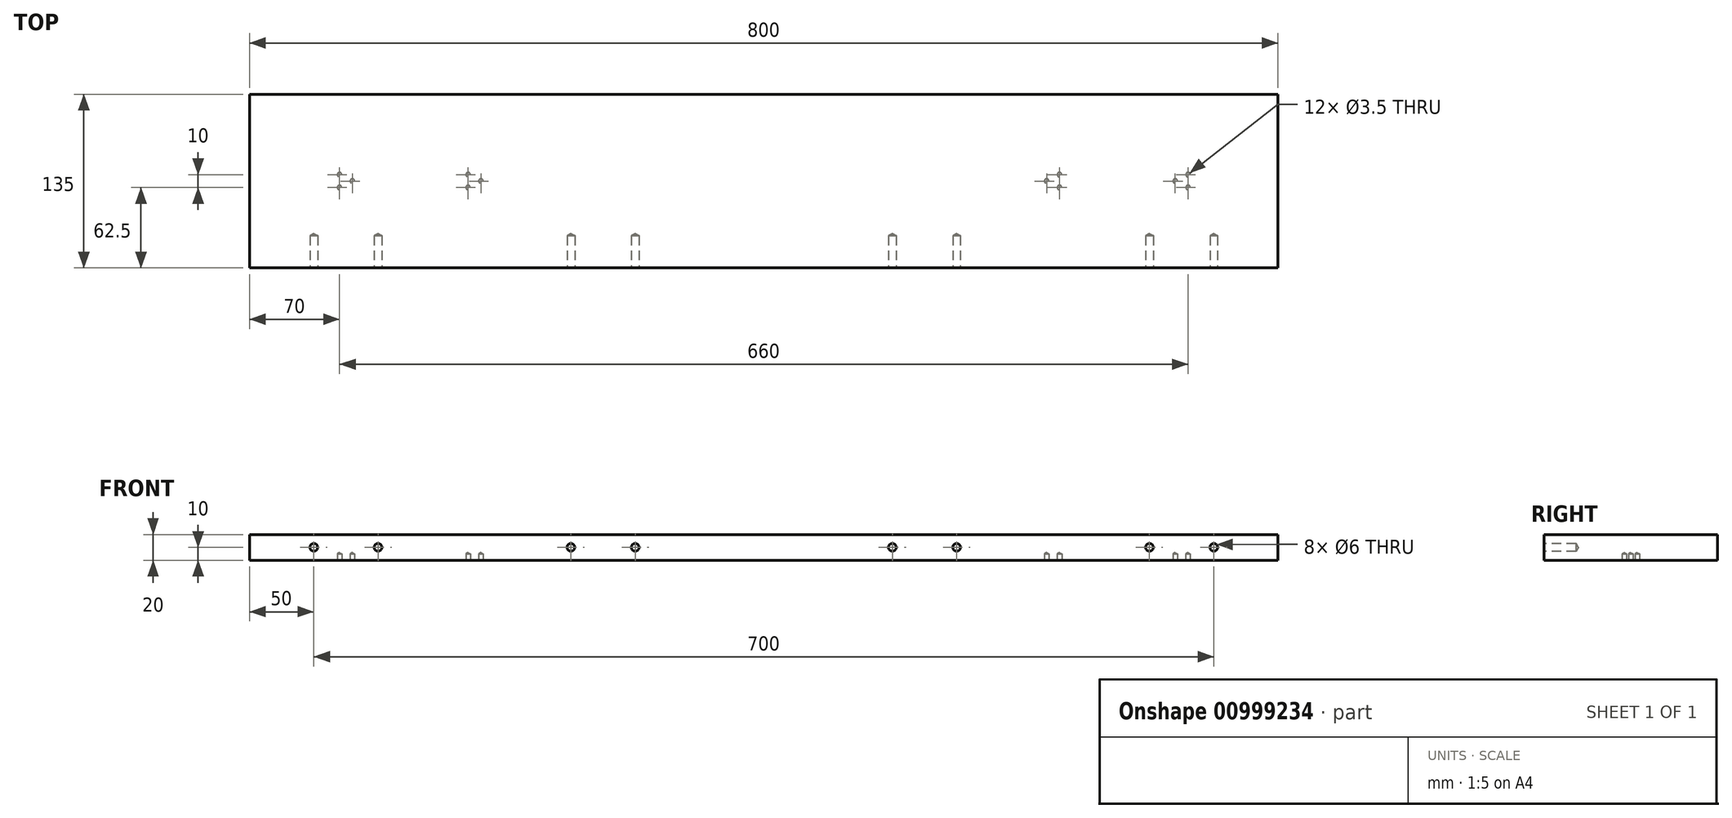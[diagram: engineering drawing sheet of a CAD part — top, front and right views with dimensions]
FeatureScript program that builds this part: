
annotation { "Feature Type Name" : "Feature", "Feature Type Description" : "" }
export const myFeature = defineFeature(function(context is Context, id is Id, definition is map)
    precondition{}
    {
        {
            var Q0;
            Q0=qCreatedBy(makeId("Top.planeOp"),FACE);
            var sketch = newSketch(context, id + "F0", { "sketchPlane" : qUnion([Q0])});
            skLineSegment(sketch, "E0.bottom", {"start": v(400, 67.5) * mm, "end": v(-400, 67.5) * mm});
            skLineSegment(sketch, "E0.top", {"start": v(400, -67.5) * mm, "end": v(-400, -67.5) * mm});
            skLineSegment(sketch, "E0.left", {"start": v(400, 67.5) * mm, "end": v(400, -67.5) * mm});
            skLineSegment(sketch, "E0.right", {"start": v(-400, 67.5) * mm, "end": v(-400, -67.5) * mm});
            skPoint(sketch, "E0.middle", {"position": v(0, 0) * mm});
            skSolve(sketch);
        }
        {
            var Q0;
            Q0=qSketchRegion(id+"F0",true);
            extrude(context, id + "F1", {"entities" : qUnion([Q0]), "endBound" : BoundingType.SYMMETRIC, "depth" : 20 * mm, "offsetDistance" : 25 * mm});
        }
        {
            var Q0;
            Q0=makeQuery(id+"F1.opExtrude","SWEPT_FACE",FACE,{"disambiguationData":[OSD([sQuery(id+"F0.wireOp",EDGE,"E0.top")])]});
            var sketch = newSketch(context, id + "F2", { "sketchPlane" : qUnion([Q0])});
            skPoint(sketch, "E1", {"position": v(-350, 0) * mm});
            skPoint(sketch, "E2", {"position": v(-100, 0) * mm});
            skPoint(sketch, "E3", {"position": v(-150, 0) * mm});
            skPoint(sketch, "E4", {"position": v(-300, 0) * mm});
            skPoint(sketch, "E5.MirrorP", {"position": v(350, 0) * mm});
            skPoint(sketch, "E6.MirrorP", {"position": v(300, 0) * mm});
            skPoint(sketch, "E7.MirrorP", {"position": v(150, 0) * mm});
            skPoint(sketch, "E8.MirrorP", {"position": v(100, 0) * mm});
            skSolve(sketch);
        }
        {
            var Q0;
            Q0=sQuery(id+"F2.wireOp",VERTEX,"E1");
            var Q1;
            Q1=sQuery(id+"F2.wireOp",VERTEX,"E4");
            var Q2;
            Q2=sQuery(id+"F2.wireOp",VERTEX,"E3");
            var Q3;
            Q3=sQuery(id+"F2.wireOp",VERTEX,"E2");
            var Q4;
            Q4=sQuery(id+"F2.wireOp",VERTEX,"E8.MirrorP");
            var Q5;
            Q5=sQuery(id+"F2.wireOp",VERTEX,"E7.MirrorP");
            var Q6;
            Q6=sQuery(id+"F2.wireOp",VERTEX,"E6.MirrorP");
            var Q7;
            Q7=sQuery(id+"F2.wireOp",VERTEX,"E5.MirrorP");
            var Q8;
            Q8=makeQuery(id+"F1.opExtrude","SWEPT_BODY",BODY,{"disambiguationData":[OSD([sQuery(id+"F0.wireOp",EDGE,"E0.bottom"),sQuery(id+"F0.wireOp",EDGE,"E0.top"),sQuery(id+"F0.wireOp",EDGE,"E0.left"),sQuery(id+"F0.wireOp",EDGE,"E0.right")])]});
            hole(context, id + "F3", {"style" : HoleStyle.SIMPLE, "endStyle" : HoleEndStyle.BLIND, "holeDiameter" : 6 * mm, "majorDiameter" : 5 * mm, "holeDepth" : 25 * mm, "isTappedThrough" : true, "tappedDepth" : 12 * mm, "tapClearance" : 3, "locations" : qUnion([Q0, Q1, Q2, Q3, Q4, Q5, Q6, Q7]), "scope" : qUnion([Q8])});
        }
        {
            var Q0;
            Q0=makeQuery(id+"F1.opExtrude","CAP_FACE",FACE,{"disambiguationData":[OSD([sQuery(id+"F0.wireOp",EDGE,"E0.bottom"),sQuery(id+"F0.wireOp",EDGE,"E0.top"),sQuery(id+"F0.wireOp",EDGE,"E0.left"),sQuery(id+"F0.wireOp",EDGE,"E0.right")])],"isStart":true});
            var sketch = newSketch(context, id + "F4", { "sketchPlane" : qUnion([Q0])});
            skPoint(sketch, "E9", {"position": v(-330, 5) * mm});
            skPoint(sketch, "E10", {"position": v(-330, -5) * mm});
            skPoint(sketch, "E11", {"position": v(-320, 0) * mm});
            skPoint(sketch, "E12", {"position": v(-230, 5) * mm});
            skPoint(sketch, "E13", {"position": v(-230, -5) * mm});
            skPoint(sketch, "E14", {"position": v(-220, 0) * mm});
            skPoint(sketch, "E15.MirrorP", {"position": v(330, 5) * mm});
            skPoint(sketch, "E16.MirrorP", {"position": v(330, -5) * mm});
            skPoint(sketch, "E17.MirrorP", {"position": v(320, 0) * mm});
            skPoint(sketch, "E18.MirrorP", {"position": v(230, 5) * mm});
            skPoint(sketch, "E19.MirrorP", {"position": v(230, -5) * mm});
            skPoint(sketch, "E20.MirrorP", {"position": v(220, 0) * mm});
            skSolve(sketch);
        }
        {
            var Q0;
            Q0=sQuery(id+"F4.wireOp",VERTEX,"E9");
            var Q1;
            Q1=sQuery(id+"F4.wireOp",VERTEX,"E10");
            var Q2;
            Q2=sQuery(id+"F4.wireOp",VERTEX,"E11");
            var Q3;
            Q3=sQuery(id+"F4.wireOp",VERTEX,"E12");
            var Q4;
            Q4=sQuery(id+"F4.wireOp",VERTEX,"E13");
            var Q5;
            Q5=sQuery(id+"F4.wireOp",VERTEX,"E14");
            var Q6;
            Q6=makeQuery(id+"F1.opExtrude","SWEPT_BODY",BODY,{"disambiguationData":[OSD([sQuery(id+"F0.wireOp",EDGE,"E0.bottom"),sQuery(id+"F0.wireOp",EDGE,"E0.top"),sQuery(id+"F0.wireOp",EDGE,"E0.left"),sQuery(id+"F0.wireOp",EDGE,"E0.right")])]});
            hole(context, id + "F5", {"style" : HoleStyle.SIMPLE, "endStyle" : HoleEndStyle.BLIND, "holeDiameter" : 3.5 * mm, "majorDiameter" : 5 * mm, "holeDepth" : 5 * mm, "isTappedThrough" : true, "tappedDepth" : 12 * mm, "tapClearance" : 3, "locations" : qUnion([Q0, Q1, Q2, Q3, Q4, Q5]), "scope" : qUnion([Q6])});
        }
        {
            var Q0;
            Q0=sQuery(id+"F4.wireOp",VERTEX,"E20.MirrorP");
            var Q1;
            Q1=sQuery(id+"F4.wireOp",VERTEX,"E19.MirrorP");
            var Q2;
            Q2=sQuery(id+"F4.wireOp",VERTEX,"E18.MirrorP");
            var Q3;
            Q3=sQuery(id+"F4.wireOp",VERTEX,"E17.MirrorP");
            var Q4;
            Q4=sQuery(id+"F4.wireOp",VERTEX,"E15.MirrorP");
            var Q5;
            Q5=sQuery(id+"F4.wireOp",VERTEX,"E16.MirrorP");
            var Q6;
            Q6=makeQuery(id+"F1.opExtrude","SWEPT_BODY",BODY,{"disambiguationData":[OSD([sQuery(id+"F0.wireOp",EDGE,"E0.bottom"),sQuery(id+"F0.wireOp",EDGE,"E0.top"),sQuery(id+"F0.wireOp",EDGE,"E0.left"),sQuery(id+"F0.wireOp",EDGE,"E0.right")])]});
            hole(context, id + "F6", {"style" : HoleStyle.SIMPLE, "endStyle" : HoleEndStyle.BLIND, "holeDiameter" : 3.5 * mm, "majorDiameter" : 5 * mm, "holeDepth" : 5 * mm, "isTappedThrough" : true, "tappedDepth" : 12 * mm, "tapClearance" : 3, "locations" : qUnion([Q0, Q1, Q2, Q3, Q4, Q5]), "scope" : qUnion([Q6])});
        }
    });
